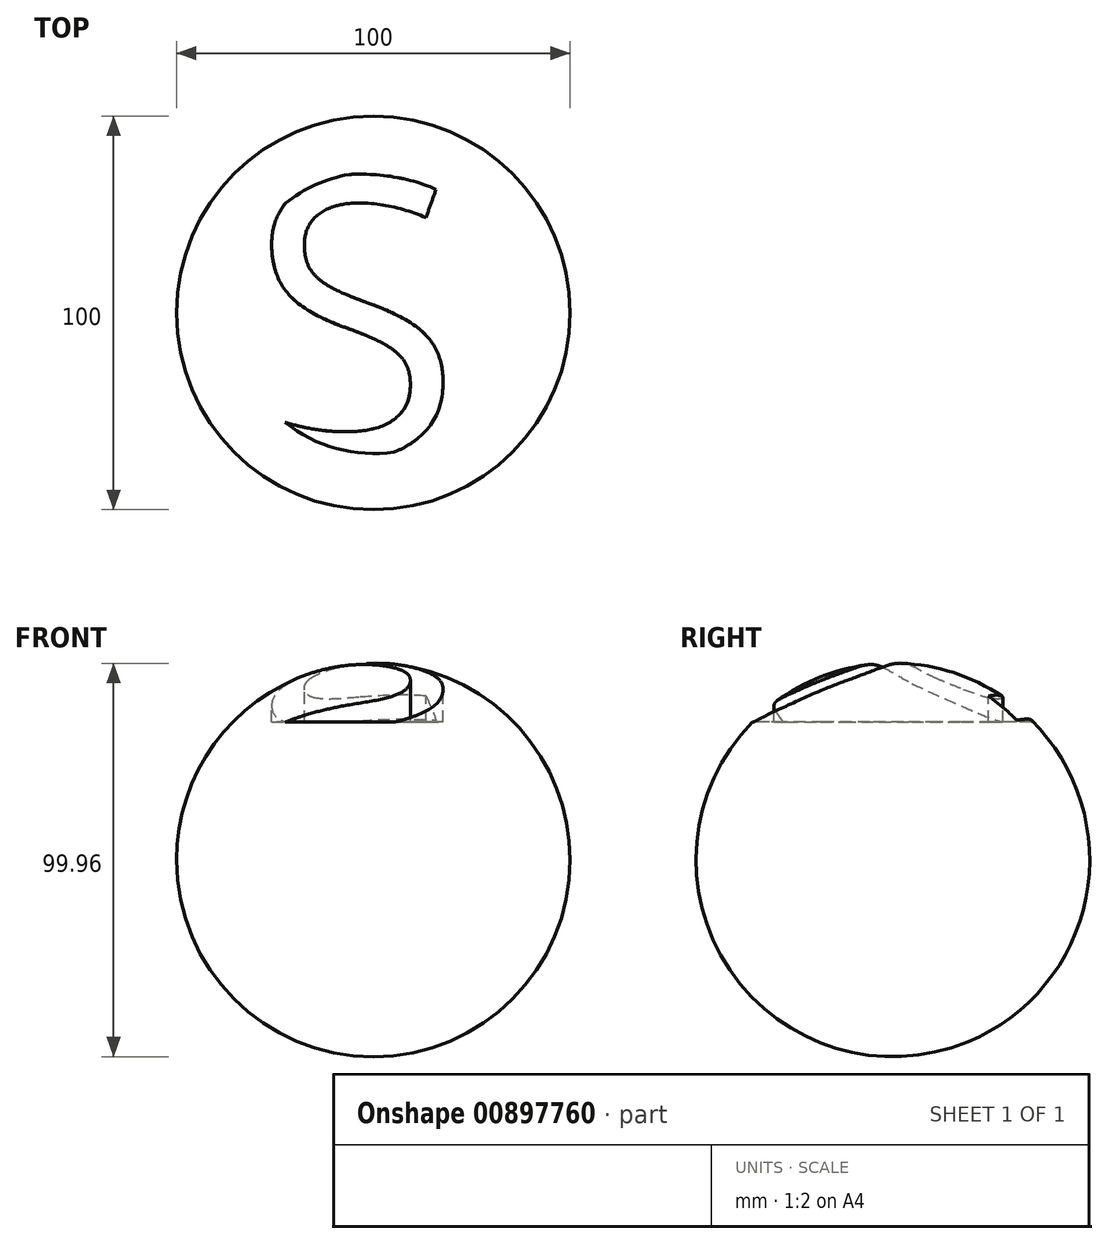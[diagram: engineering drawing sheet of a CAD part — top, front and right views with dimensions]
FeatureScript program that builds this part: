
annotation { "Feature Type Name" : "Feature", "Feature Type Description" : "" }
export const myFeature = defineFeature(function(context is Context, id is Id, definition is map)
    precondition{}
    {
        {
            var Q0;
            Q0=qCreatedBy(makeId("Top.planeOp"),FACE);
            var sketch = newSketch(context, id + "F0", { "sketchPlane" : qUnion([Q0])});
            skCircle(sketch, "E0", {"center": v(0, 0) * mm, "radius": 50 * mm});
            skLineSegment(sketch, "E1", {"start": v(74.09, 0) * mm, "end": v(-76.08, 0) * mm});
            skSolve(sketch);
        }
        {
            var Q0;
            {var subQ0=sQuery(id+"F0.wireOp",EDGE,"E1");var subQ1=sQuery(id+"F0.wireOp",EDGE,"E0");var subQ2=makeQuery(id+"F0.imprint","INTERSECT",VERTEX,{"disambiguationData":[OD(0.0)],"derivedFrom":[subQ1,subQ0]});Q0=makeQuery(id+"F0.imprint","IMPRINT",FACE,{"disambiguationData":[TD([[makeQuery(id+"F0.imprint","IMPRINT",EDGE,{"disambiguationData":[TD([[subQ2,1.0]])],"derivedFrom":subQ1}),1.0]])]});}
            var Q1;
            Q1=sQuery(id+"F0.wireOp",EDGE,"E1");
            revolve(context, id + "F1", {"surfaceOperationType" : NewSurfaceOperationType.NEW, "entities" : qUnion([Q0]), "axis" : qUnion([Q1]), "revolveType" : RevolveType.FULL});
        }
        {
            var Q0;
            Q0=qCreatedBy(makeId("Top.planeOp"),FACE);
            cPlane(context, id + "F2", {"entities" : qUnion([Q0]), "cplaneType" : CPlaneType.OFFSET, "offset" : 50 * mm, "width" : 150 * mm, "height" : 150 * mm});
        }
        {
            var Q0;
            Q0=qCreatedBy(id+"F2.planeOp",FACE);
            var sketch = newSketch(context, id + "F3", { "sketchPlane" : qUnion([Q0])});
            skText(sketch, "E2", { "text": "S", "fontName": "OpenSans-Regular.ttf"});
            const initialGuessF3  = {"E2": [-0.03187, -0.03642, 1, 0, 0.07128]};
            skSetInitialGuess(sketch, initialGuessF3);
            skSolve(sketch);
        }
        {
            var Q0;
            Q0 = qSketchRegion(id + "F3", true);
            extrude(context, id + "F4", {"entities" : qUnion([Q0]), "operationType" : NewBodyOperationType.REMOVE, "oppositeDirection" : true, "depth" : 15 * mm, "offsetDistance" : 25 * mm});
        }
    });
